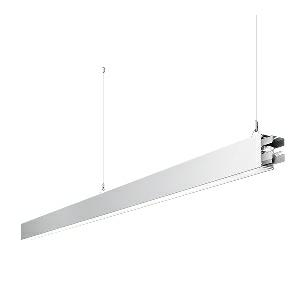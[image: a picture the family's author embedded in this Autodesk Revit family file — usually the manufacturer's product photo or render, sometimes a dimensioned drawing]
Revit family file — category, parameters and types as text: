
# Revit family: idoo_line_-_ilp_6000_840_d_mid_00805703_fbcd
name_source: partatom
category: Lighting Fixtures
units: mm (PartAtom-declared; Revit-internal decimal feet)

## family parameters
Cut with Voids When Loaded = No
Host = Face
Light Source = No
Part Type = Normal
Room Calculation Point = No
Round Connector Dimension = Use Diameter
Shared = No

## types (1)
- IDOO.line - ILP 6000/840/D MID (1 x LED, 6300 lm, 4000K)
    Apparent Load = 46 VA
    Approval mark = CE
    CIE Flux Codes = 66 91 98 40 100
    Color Rendering = 80-89
    Color Temperature = 4000K
    Control Gear = Electronic ballast
    Default Elevation = 1800 mm
    Description = ILP 6000/840/D|Suspended luminaire|light source: LED|connected load: 220-240 V, 50/60 Hz|Power consumption: approx. 46 W|standby: approx. 0,15|luminous flux: 6300 lm|luminous efficacy: 136 lm/W|light distribution: Direct/indirect|direct ratio: approx. 40 %|colour temperature: Cold white, ca. 4000 K|color rendering index (CRI): >= 80|chromaticity tolerance:  3 SDCM|System of protection: IP 40|technology: Continuously dimmable|luminaire body|material: Sectional aluminium|colour: White|lamp cover: Acrylic (PMMA), Clear|mains lead: 1,0 m With free stranded wires|Fastening: Steel cable 0.3 - 0.7 m|glare control: Prism aperture|luminance(L65): <= 2700 cd/m|unified glare rating(4H 8H): <=  16|special features: DALI Load 1x, TouchDIM - dimming via standard switch, Through-wired, up to 18 m on one mains connection, Flicker-free, Suitable as emergency lighting, Mechanical and electrical connection of the individual modules without tools|
    Frequency = 50 Hz
    Height = 110 mm
    Lamp = 1 x LED
    Lamp Light Flux = 6300 lm
    Lamp count = 1
    Length = 2244 mm
    Luminous efficacy = 137 lm/W
    Manufacturer = Waldmann
    ModVariant = No
    Model = 00805703
    Mounting Place = Ceiling
    Mounting Type = Pendant
    Number of Poles = 1
    OnlyDefault = Yes
    Power Factor = 1
    Product Name = IDOO.line - ILP 6000/840/D MID
    Product group = Suspended luminaire
    ProductGroupID = 9
    Protection Class = Protection class I
    Protection Degree = IP 40
    RLX_Detail_Level = 1
    RLX_Emergency_Light_Flux = 0 lm
    RLX_Emergency_Type = 0
    RLX_Emergency_Type_DB = No
    RlxData = <blob elided: 22109 chars, md5=018df3a9>
    Socket = socket
    Standby Power = 0 W
    System Light Flux = 6300 lm
    System Power = 46 W
    Type Comments = Product without accessories
    Type Image = 113314000-00692606.jpg
    URL = http://relux.com
    VarID = ---
    Voltage = 230 V
    Voltage Range = 220-240 V
    Weight = 0.00 kg
    Width = 60 mm  [stored 0.19685 ft]

note: [stored X ft] marks values corroborated as IEEE doubles in the binary element streams (Revit-internal decimal feet)

## geometry (parser evidence)
native form markers: Blend x4, Sweep x14
no freeform markers — native parametric forms only
